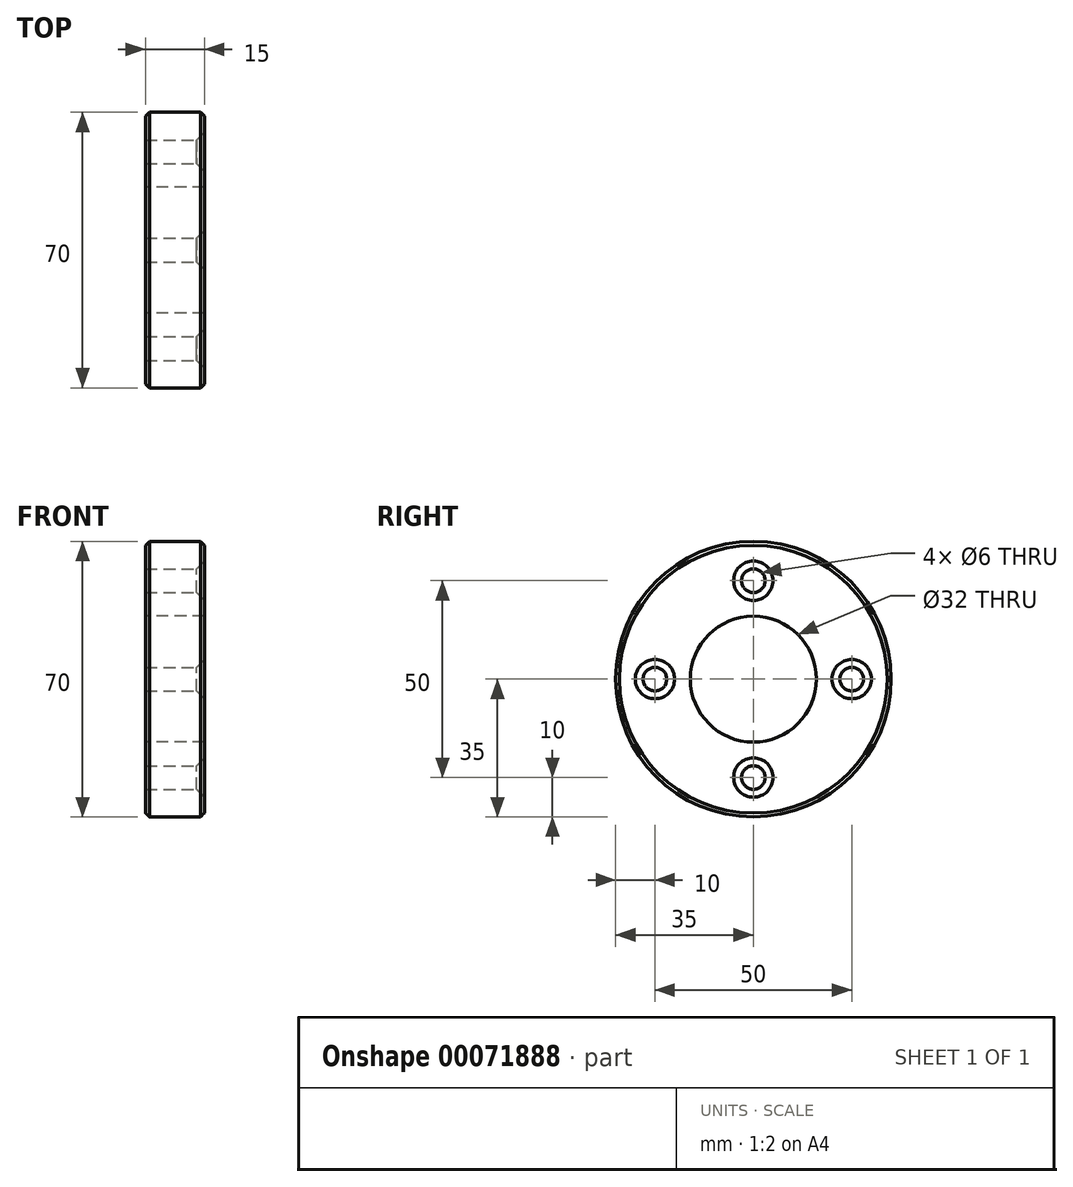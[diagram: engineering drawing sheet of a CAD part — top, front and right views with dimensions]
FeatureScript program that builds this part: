
annotation { "Feature Type Name" : "Feature", "Feature Type Description" : "" }
export const myFeature = defineFeature(function(context is Context, id is Id, definition is map)
    precondition{}
    {
        {
            var Q0;
            Q0=qCreatedBy(makeId("Right.planeOp"),FACE);
            var sketch = newSketch(context, id + "F0", { "sketchPlane" : qUnion([Q0])});
            skCircle(sketch, "E0", {"center": v(0, 0) * mm, "radius": 35 * mm});
            skCircle(sketch, "E1", {"center": v(0, 0) * mm, "radius": 16 * mm});
            skSolve(sketch);
        }
        {
            var Q0;
            Q0 = qSketchRegion(id + "F0", true);
            extrude(context, id + "F1", {"entities" : qUnion([Q0]), "depth" : 15 * mm});
        }
        {
            var Q0;
            Q0=makeQuery(id+"F1.opExtrude","CAP_EDGE",EDGE,{"disambiguationData":[OSD([sQuery(id+"F0.wireOp",EDGE,"E0")])],"isStart":false});
            var Q1;
            Q1=makeQuery(id+"F1.opExtrude","CAP_EDGE",EDGE,{"disambiguationData":[OSD([sQuery(id+"F0.wireOp",EDGE,"E0")])],"isStart":true});
            chamfer(context, id + "F2", {"entities" : qUnion([Q0, Q1]), "width" : 1 * mm, "tangentPropagation" : true});
        }
        {
            var Q0;
            Q0=makeQuery(id+"F1.opExtrude","CAP_FACE",FACE,{"disambiguationData":[OSD([sQuery(id+"F0.wireOp",EDGE,"E0"),sQuery(id+"F0.wireOp",EDGE,"E1")])],"isStart":false});
            var sketch = newSketch(context, id + "F3", { "sketchPlane" : qUnion([Q0])});
            skCircle(sketch, "E2", {"center": v(0, 0) * mm, "radius": 25 * mm, "construction": true});
            skLineSegment(sketch, "E3", {"start": v(0, 35.95) * mm, "end": v(0, -41.43) * mm, "construction": true});
            skLineSegment(sketch, "E4", {"start": v(38.1, 0) * mm, "end": v(-38.88, 0) * mm, "construction": true});
            skPoint(sketch, "E5", {"position": v(0, 25) * mm});
            skPoint(sketch, "E6", {"position": v(-25, 0) * mm});
            skPoint(sketch, "E7", {"position": v(25, 0) * mm});
            skPoint(sketch, "E8", {"position": v(0, -25) * mm});
            skSolve(sketch);
        }
        {
            var Q0;
            Q0=sQuery(id+"F3.wireOp",VERTEX,"E5");
            var Q1;
            Q1=sQuery(id+"F3.wireOp",VERTEX,"E6");
            var Q2;
            Q2=sQuery(id+"F3.wireOp",VERTEX,"E7");
            var Q3;
            Q3=sQuery(id+"F3.wireOp",VERTEX,"E8");
            var Q4;
            Q4=makeQuery(id+"F1.opExtrude","SWEPT_BODY",BODY,{"disambiguationData":[OSD([sQuery(id+"F0.wireOp",EDGE,"E0"),sQuery(id+"F0.wireOp",EDGE,"E1")])]});
            hole(context, id + "F4", {"style" : HoleStyle.C_SINK, "holeDiameter" : 6 * mm, "cSinkDiameter" : 10 * mm, "endStyle" : HoleEndStyle.THROUGH, "locations" : qUnion([Q0, Q1, Q2, Q3]), "scope" : qUnion([Q4]), "cSinkAngle" : 90 * degree});
        }
    });
